# Revit family: P7267-3030K9
name_source: partatom
category: Lighting Fixtures
revit_build: Autodesk Revit 2014 (Build: 20130308_1515(x64)
units: mm (PartAtom-declared; Revit-internal decimal feet)

## types (1)
- P7267-3030K9
    Apparent Load = 20 VA
    Assembly Code = D5020200
    Color Filter = 16777215
    Connector Description = Lighting Connector
    Default Elevation = 48"
    Description = Integrated 4ft strip light. Great for utility rooms, garages and workrooms. Long lasting LED lights. 2912 lumens, 78 lumens per watt (delivered). 3000K ENERGY STAR.
    Dimming Lamp Color Temperature Shift = <None>
    Emit Shape Visible in Rendering = No
    Emit from Rectangle Length = 46 1/2"
    Emit from Rectangle Width = 1 3/4"
    Features = White finish
2912 lumens, 78 lumens per watt (delivered)
3000K, 90CRI
LED's integral to fixture
Ceiling mount
Dimmable to 10% with many Forward Phase (Triac) or Reverse Phase (ELV) dimmers
Damp location listed
Energy Star Qualified
Meets California T24 JA8-2016.
Suitable for use in clothes closets when installed in accordance with the NEC 410.16 spacing requirements.
    Fixture distribution = Direct
    Glass = Hubbell - Glass
    Height = 1 7/8"
    Housing Material = Paint - Hubbell - White Texture
    Inner Length = 7 7/8"
    Lamp = LED
    Length = 46 1/2"
    Load Classification = Lighting
    Manufacturer = Progress Lighting
    Model = P7267 4FT LED STRIP
    Mounting = Paint - Hubbell - Light Silver
    Photometric Web File = PROG_P7267-3030K9_17.02851_testlabreports.ies
    Power Factor = 1
    Product Documentation Link = https://hubbellcdn.com
    Product Link = https://www.hubbell.com
    Reflector Finish = Hubbell - White Glass
    Tilt Angle = -90.00°
    URL = https://www.hubbell.com
    Voltage = 120 V
    Warranty = 5 years Warranty
    Wattage Comments = 20W
    Watts = 20 W
    Width = 1 3/4"
    Wings = Paint - Hubbell - Light Silver

## geometry (parser evidence)
native form markers: Sweep x4
no freeform markers — native parametric forms only
